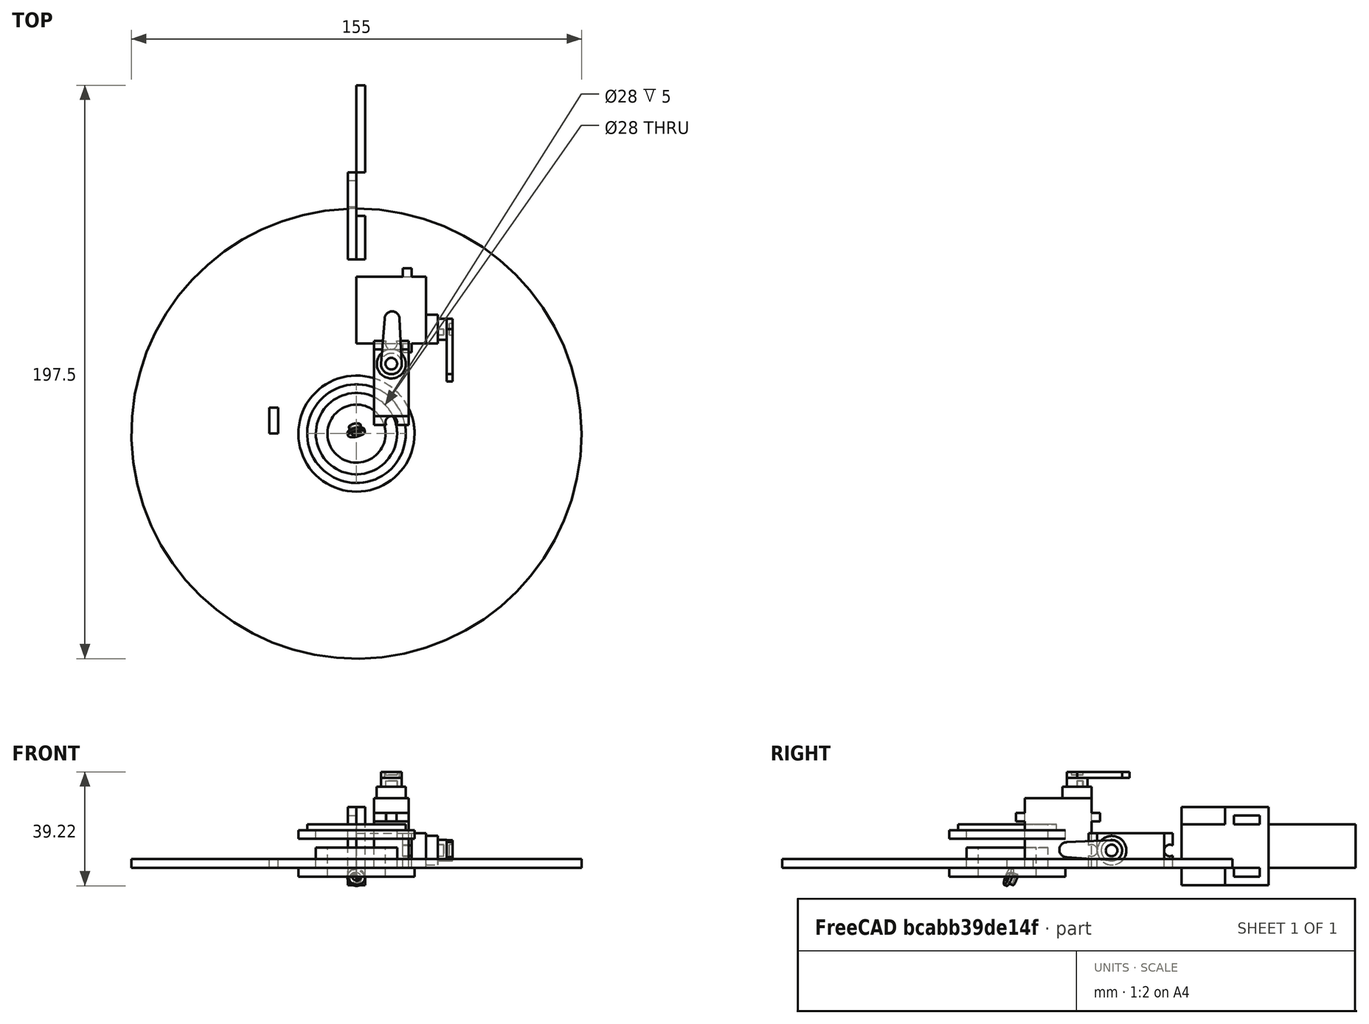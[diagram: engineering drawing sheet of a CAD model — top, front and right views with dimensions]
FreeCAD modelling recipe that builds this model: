
FCSTD DOCUMENT  (FreeCAD 0.16R6707 (Git))
Label: turret
License: All rights reserved
LicenseURL: http://en.wikipedia.org/wiki/All_rights_reserved
objects: Part::Cylinder×21, Part::Box×17, Part::Cut×10, Part::MultiFuse×9, PartDesign::Pocket×2
note: 61 computed .brp shape members not serialized (recipe doc carries the construction recipe); baked Part::Feature solids carry a one-line shape summary decoded from their .brp

FEATURE [Part::Box] Box071  label="Würfel071"
  Height = 16
  Length = 12
  Width = 23
FEATURE [Part::Box] Box072  label="Würfel072"
  Height = 3
  Length = 12
  Placement = pos=(0,-3,16) rot=(0,0,1;0rad)
  Width = 29
FEATURE [Part::Box] Box073  label="Würfel073"
  Height = 5
  Length = 12
  Placement = pos=(0,0,19) rot=(0,0,1;0rad)
  Width = 23
FEATURE [Part::Cylinder] Cylinder007  label="Zylinder007"
  Angle = 360
  Height = 4
  Placement = pos=(6,-2,16) rot=(0,0,1;0rad)
  Radius = 2
FEATURE [Part::Cylinder] Cylinder008  label="Zylinder008"
  Angle = 360
  Height = 4
  Placement = pos=(6,25,16) rot=(0,0,1;0rad)
  Radius = 2
FEATURE [Part::Cut] Cut027
  Base = -> Box072
  Tool = -> Cylinder007
FEATURE [Part::Cut] Cut028
  Base = -> Cut027
  Tool = -> Cylinder008
FEATURE [Part::Cylinder] Cylinder009  label="Zylinder009"
  Angle = 360
  Height = 4
  Placement = pos=(6,18,24) rot=(0,0,1;0rad)
  Radius = 5
FEATURE [Part::Cylinder] Cylinder010  label="Zylinder010"
  Angle = 360
  Height = 8
  Placement = pos=(6,18,24) rot=(0,0,1;0rad)
  Radius = 2
FEATURE [Part::Cylinder] Cylinder011  label="Zylinder011"
  Angle = 360
  Height = 2
  Placement = pos=(6,18,30) rot=(0,0,1;0rad)
  Radius = 2.5
FEATURE [Part::MultiFuse] Fusion020
  Shapes = -> [Cylinder009,Cylinder010,Cylinder011]
FEATURE [PartDesign::Pocket] Pocket001
  Length = 5
  Placement = pos=(1,33.5,31) rot=(0,0,1;1.5708rad)
  Type = 1
FEATURE [Part::MultiFuse] Fusion021  label="Servo001"
  Placement = pos=(0,54,0) rot=(0.707107,0,0.707107;3.14159rad)
  Shapes = -> [Pocket001,Fusion020,Cut028,Box073,Box071]
FEATURE [Part::Box] Box074  label="Würfel074"
  Height = 16
  Length = 12
  Width = 23
FEATURE [Part::Box] Box075  label="Würfel075"
  Height = 3
  Length = 12
  Placement = pos=(0,-3,16) rot=(0,0,1;0rad)
  Width = 29
FEATURE [Part::Box] Box076  label="Würfel076"
  Height = 5
  Length = 12
  Placement = pos=(0,0,19) rot=(0,0,1;0rad)
  Width = 23
FEATURE [Part::Cylinder] Cylinder012  label="Zylinder012"
  Angle = 360
  Height = 4
  Placement = pos=(6,-2,16) rot=(0,0,1;0rad)
  Radius = 2
FEATURE [Part::Cylinder] Cylinder013  label="Zylinder013"
  Angle = 360
  Height = 4
  Placement = pos=(6,25,16) rot=(0,0,1;0rad)
  Radius = 2
FEATURE [Part::Cut] Cut029
  Base = -> Box075
  Tool = -> Cylinder012
FEATURE [Part::Cut] Cut030
  Base = -> Cut029
  Tool = -> Cylinder013
FEATURE [Part::Cylinder] Cylinder014  label="Zylinder014"
  Angle = 360
  Height = 4
  Placement = pos=(6,18,24) rot=(0,0,1;0rad)
  Radius = 5
FEATURE [Part::Cylinder] Cylinder015  label="Zylinder015"
  Angle = 360
  Height = 8
  Placement = pos=(6,18,24) rot=(0,0,1;0rad)
  Radius = 2
FEATURE [Part::Cylinder] Cylinder016  label="Zylinder016"
  Angle = 360
  Height = 2
  Placement = pos=(6,18,30) rot=(0,0,1;0rad)
  Radius = 2.5
FEATURE [Part::MultiFuse] Fusion022
  Shapes = -> [Cylinder014,Cylinder015,Cylinder016]
FEATURE [PartDesign::Pocket] Pocket002
  Length = 5
  Placement = pos=(1,33.5,31) rot=(0,0,1;1.5708rad)
  Type = 1
FEATURE [Part::MultiFuse] Fusion  label="Servo002"
  Placement = pos=(6,6,0) rot=(0,0,1;0rad)
  Shapes = -> [Pocket002,Fusion022,Cut030,Box076,Box074]
FEATURE [Part::Box] Box040  label="Würfel040"
  Height = 15
  Length = 3
  Placement = pos=(30,60,0) rot=(0,0,1;0rad)
  Width = 30
FEATURE [Part::Box] Box041  label="Würfel041"
  Height = 6
  Length = 3
  Width = 15
FEATURE [Part::Box] Box042  label="Würfel042"
  Height = 3
  Length = 3
  Placement = pos=(0,3,0) rot=(0,0,1;0rad)
  Width = 9
FEATURE [Part::Cut] Cut013  label="Loop004"
  Base = -> Box041
  Placement = pos=(30,75,15) rot=(0,0,1;0rad)
  Tool = -> Box042
FEATURE [Part::Box] Box043  label="Würfel043"
  Height = 6
  Length = 3
  Width = 15
FEATURE [Part::Box] Box044  label="Würfel044"
  Height = 3
  Length = 3
  Placement = pos=(0,3,0) rot=(0,0,1;0rad)
  Width = 9
FEATURE [Part::Cut] Cut014  label="Loop005"
  Base = -> Box043
  Placement = pos=(33,75,0) rot=(0,1,0;3.14159rad)
  Tool = -> Box044
FEATURE [Part::MultiFuse] Fusion010  label="SidePlate002"
  Placement = pos=(-33,0,0) rot=(0,0,1;0rad)
  Shapes = -> [Box040,Cut013,Cut014]
FEATURE [Part::Box] Box  label="Cube"
  Height = 6
  Length = 3
  Placement = pos=(0,60,15) rot=(0,0,1;0rad)
  Width = 15
FEATURE [Part::Box] Box077  label="Cube001"
  Height = 6
  Length = 3
  Placement = pos=(0,60,-6) rot=(0,0,1;0rad)
  Width = 15
FEATURE [Part::Box] Box078  label="Cube002"
  Height = 6
  Length = 3
  Placement = pos=(-3,60,15) rot=(0,0,1;0rad)
  Width = 15
FEATURE [Part::Box] Box079  label="Cube003"
  Height = 6
  Length = 3
  Placement = pos=(-3,60,-6) rot=(0,0,1;0rad)
  Width = 15
FEATURE [Part::MultiFuse] Fusion023
  Shapes = -> [Box079,Box078,Fusion010]
FEATURE [Part::Box] Box080  label="Cube004"
  Height = 15
  Length = 3
  Placement = pos=(0,90,0) rot=(0,0,1;0rad)
  Width = 30
FEATURE [Part::Cylinder] Cylinder
  Angle = 360
  Height = 3
  Radius = 77.5
FEATURE [Part::Box] Box081  label="Cube005"
  Height = 3
  Length = 3
  Placement = pos=(-30,0,0) rot=(0,0,1;0rad)
  Width = 9
FEATURE [Part::Cylinder] Cylinder017  label="Cylinder001"
  Angle = 360
  Height = 3
  Radius = 14
FEATURE [Part::Cut] Cut
  Base = -> Cylinder
  Tool = -> Cylinder017
FEATURE [Part::Cylinder] Cylinder018  label="Cylinder002"
  Angle = 360
  Height = 3
  Radius = 20
FEATURE [Part::Cylinder] Cylinder019  label="Cylinder003"
  Angle = 360
  Height = 5
  Radius = 17
FEATURE [Part::MultiFuse] Fusion024
  Shapes = -> [Cylinder019,Cylinder018]
FEATURE [Part::Cylinder] Cylinder020  label="Cylinder004"
  Angle = 360
  Height = 5
  Radius = 14
FEATURE [Part::Cut] Cut031
  Base = -> Fusion024
  Placement = pos=(0,0,10) rot=(0,0,1;0rad)
  Tool = -> Cylinder020
FEATURE [Part::Cylinder] Cylinder021  label="Cylinder005"
  Angle = 360
  Height = 3
  Radius = 20
FEATURE [Part::Cylinder] Cylinder022  label="Cylinder006"
  Angle = 360
  Height = 10
  Radius = 14
FEATURE [Part::MultiFuse] Fusion025
  Shapes = -> [Cylinder021,Cylinder022]
FEATURE [Part::Cylinder] Cylinder023  label="Cylinder007"
  Angle = 360
  Height = 10
  Radius = 10
FEATURE [Part::Cut] Cut032
  Base = -> Fusion025
  Placement = pos=(0,0,-3) rot=(0,0,1;0rad)
  Tool = -> Cylinder023
FEATURE [Part::Cylinder] Cylinder024  label="Cylinder028"
  Angle = 360
  Height = 1
  Radius = 3
FEATURE [Part::Cylinder] Cylinder025  label="Cylinder029"
  Angle = 360
  Height = 3
  Radius = 2
FEATURE [Part::MultiFuse] Fusion026
  Shapes = -> [Cylinder024,Cylinder025]
FEATURE [Part::Cylinder] Cylinder026  label="Cylinder030"
  Angle = 360
  Height = 3
  Radius = 1.5
FEATURE [Part::Cut] Cut033  label="3mmLager"
  Base = -> Fusion026
  Placement = pos=(3.14645e-06,-2.49643e-06,-3) rot=(-0.210878,0.793695,0.570595;3.10374rad)
  Tool = -> Cylinder026
